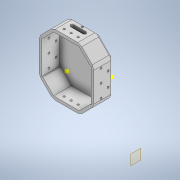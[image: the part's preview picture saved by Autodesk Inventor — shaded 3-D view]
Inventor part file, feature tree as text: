
AUTODESK INVENTOR PART (.ipt)
format: ipt  version: 2022 (Build 260153000, 153)  size: 318,464 bytes
history: native  units: in
note: dims shown in document units (in); Inventor stores cm internally (conversion verified against a paired STEP export)
features: extrude x8, sketch x8, chamfer x2, projected_geometry x2, plane x1
ambient origin geometry x8: Origin, YZ Plane, XZ Plane, XY Plane, X Axis, Y Axis, Z Axis, Center Point
bodies: Solid1 (feature_tree)
feature tree (21):
  extrude  "Extrusion1"  Depth=1.4961in TaperAngle=0.0deg
  extrude  "Extrusion2"  Depth=0.1575in
  plane  "Work Plane1"
  extrude  "Extrusion4"  TaperAngle=0.0deg  [1 undecoded]
  chamfer  "Chamfer1"  Distance=0.0787in Angle=45.0deg
  chamfer  "Chamfer2"  Distance=0.0787in Angle=45.0deg
  extrude  "Extrusion5"  Depth=1.378in
  extrude  "Extrusion6"  Depth=0.3937in TaperAngle=0.0deg
  sketch  "Sketch10"  dims[d32=45.0deg d33=0.3937in d34=0.0in]
  extrude  "Extrusion7"  Depth=0.3937in
  extrude  "Extrusion8"  Depth=0.1575in
  extrude  "Extrusion9"  Depth=0.1575in
  sketch  "Sketch14"  dims[d37=1.1811in d38=0.1575in]
  sketch  "Sketch15"  dims[d39=0.1575in d40=0.1575in d41=0.0in d42=0.0in d44=0.315in d45=0.315in d46=0.315in d50=0.0098in d51=0.0in d52=0.0197in d53=0.0in d54=1.5945in d55=0.0in d56=0.0787in d57=0.0787in d58=0.0787in d59=0.1575in]
  sketch  "Sketch2"  dims[d2=0.2362in d3=1.4961in d4=0.0in]
  projected_geometry  "Projected Loop1"
  sketch  "Sketch7"  dims[d5=0.1181in d6=0.0in d17=0.1575in d18=0.1575in]
  sketch  "Sketch8"  dims[d19=0.5906in d20=0.0in d21=0.0in d22=0.1969in d23=0.0787in d24=45.0deg d25=0.1969in d26=0.0787in d27=45.0deg]
  sketch  "Sketch9"  dims[d30=0.6299in d31=1.378in]
  sketch  "Sketch11"  dims[d35=0.3937in d36=0.5906in]
  projected_geometry  "Projected Loop2"
note: 1 required parameter value undecoded (feature->parameter linkage not recoverable at this tier; creation-order binding heuristic only, values carry confidence <= 0.55)
